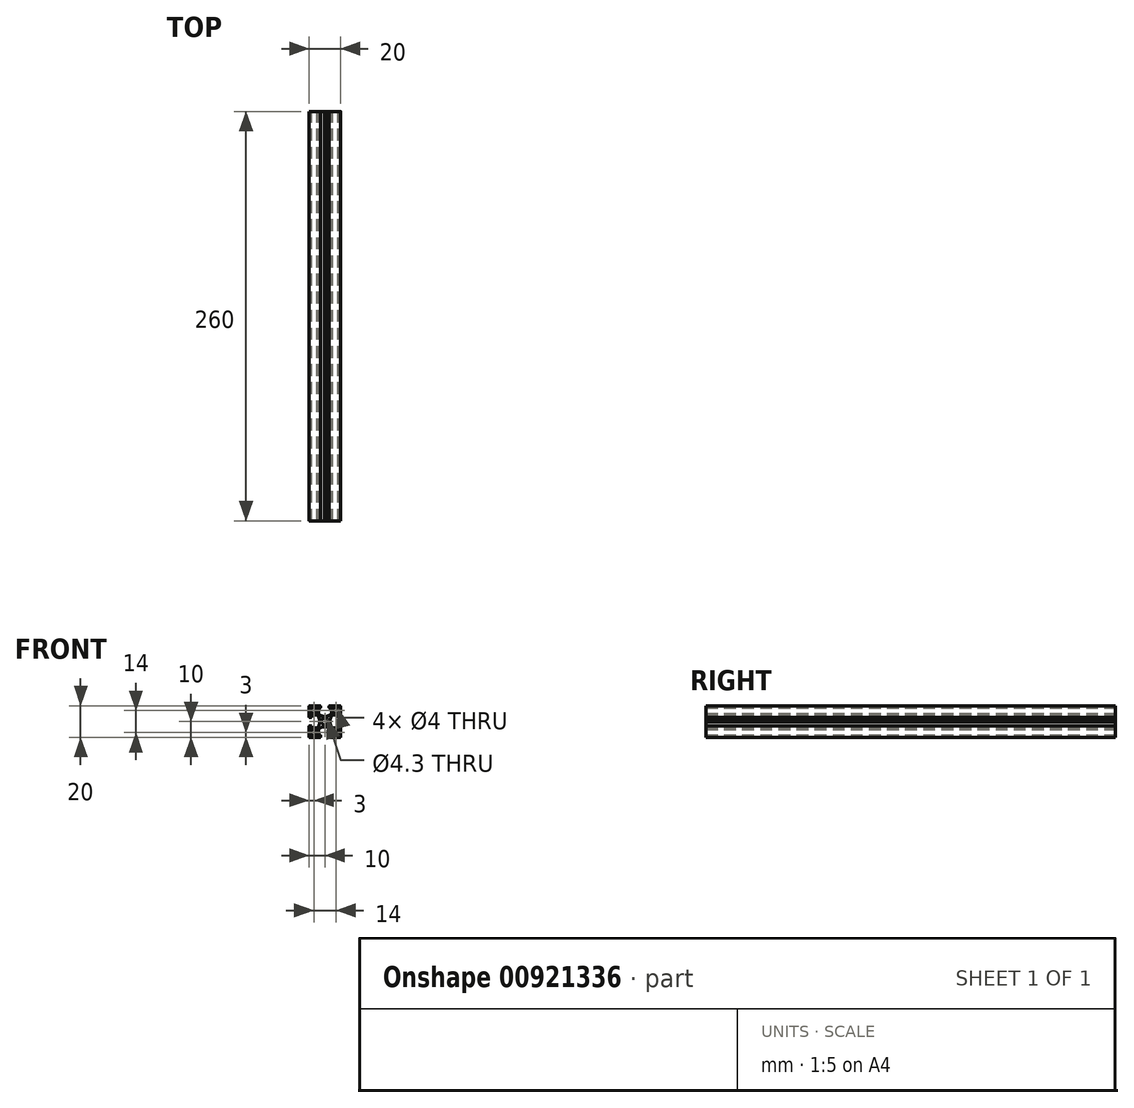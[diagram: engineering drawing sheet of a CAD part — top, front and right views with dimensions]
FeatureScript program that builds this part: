
annotation { "Feature Type Name" : "Feature", "Feature Type Description" : "" }
export const myFeature = defineFeature(function(context is Context, id is Id, definition is map)
    precondition{}
    {
        {
            var Q0;
            Q0=qCreatedBy(makeId("Front.planeOp"),FACE);
            var sketch = newSketch(context, id + "F0", { "sketchPlane" : qUnion([Q0])});
            skLineSegment(sketch, "E0", {"start": v(-11.2, 0) * mm, "end": v(11.2, 0) * mm});
            skCircle(sketch, "E1", {"center": v(0, 0) * mm, "radius": 2.15 * mm});
            skLineSegment(sketch, "E2", {"start": v(4.15, 4.94) * mm, "end": v(4.15, 8.2) * mm});
            skArc(sketch, "E3", {"start": v(4.15, 8.2) * mm, "mid": v(4.06, 8.41) * mm, "end": v(3.85, 8.5) * mm});
            skLineSegment(sketch, "E4", {"start": v(3.85, 8.5) * mm, "end": v(2.95, 8.5) * mm});
            skArc(sketch, "E5", {"start": v(2.95, 8.5) * mm, "mid": v(2.74, 8.59) * mm, "end": v(2.65, 8.8) * mm});
            skLineSegment(sketch, "E6", {"start": v(2.65, 8.8) * mm, "end": v(2.65, 9.7) * mm});
            skArc(sketch, "E7", {"start": v(2.65, 9.7) * mm, "mid": v(2.74, 9.91) * mm, "end": v(2.95, 10) * mm});
            skLineSegment(sketch, "E8", {"start": v(2.95, 10) * mm, "end": v(9.7, 10) * mm});
            skArc(sketch, "E9", {"start": v(9.7, 10) * mm, "mid": v(9.91, 9.91) * mm, "end": v(10, 9.7) * mm});
            skLineSegment(sketch, "E10", {"start": v(10, 9.7) * mm, "end": v(10, 2.95) * mm});
            skArc(sketch, "E11", {"start": v(10, 2.95) * mm, "mid": v(9.91, 2.74) * mm, "end": v(9.7, 2.65) * mm});
            skLineSegment(sketch, "E12", {"start": v(9.7, 2.65) * mm, "end": v(8.8, 2.65) * mm});
            skArc(sketch, "E13", {"start": v(8.8, 2.65) * mm, "mid": v(8.59, 2.74) * mm, "end": v(8.5, 2.95) * mm});
            skLineSegment(sketch, "E14", {"start": v(8.5, 2.95) * mm, "end": v(8.5, 3.85) * mm});
            skArc(sketch, "E15", {"start": v(8.5, 3.85) * mm, "mid": v(8.41, 4.06) * mm, "end": v(8.2, 4.15) * mm});
            skLineSegment(sketch, "E16", {"start": v(8.2, 4.15) * mm, "end": v(4.94, 4.15) * mm});
            skArc(sketch, "E17", {"start": v(4.94, 4.15) * mm, "mid": v(4.81, 4.12) * mm, "end": v(4.7, 4.04) * mm});
            skArc(sketch, "E18", {"start": v(4.7, 4.04) * mm, "mid": v(3.71, 2.28) * mm, "end": v(3.3, 0.3) * mm});
            skLineSegment(sketch, "E19", {"start": v(3.3, 0.3) * mm, "end": v(3, 0) * mm});
            skLineSegment(sketch, "E20", {"start": v(3, 0) * mm, "end": v(3.3, -0.3) * mm});
            skArc(sketch, "E21", {"start": v(3.3, -0.3) * mm, "mid": v(3.71, -2.28) * mm, "end": v(4.7, -4.04) * mm});
            skArc(sketch, "E22", {"start": v(4.7, -4.04) * mm, "mid": v(4.81, -4.12) * mm, "end": v(4.94, -4.15) * mm});
            skLineSegment(sketch, "E23", {"start": v(4.94, -4.15) * mm, "end": v(8.2, -4.15) * mm});
            skArc(sketch, "E24", {"start": v(8.2, -4.15) * mm, "mid": v(8.41, -4.06) * mm, "end": v(8.5, -3.85) * mm});
            skLineSegment(sketch, "E25", {"start": v(8.5, -3.85) * mm, "end": v(8.5, -2.95) * mm});
            skArc(sketch, "E26", {"start": v(8.5, -2.95) * mm, "mid": v(8.59, -2.74) * mm, "end": v(8.8, -2.65) * mm});
            skLineSegment(sketch, "E27", {"start": v(8.8, -2.65) * mm, "end": v(9.7, -2.65) * mm});
            skArc(sketch, "E28", {"start": v(9.7, -2.65) * mm, "mid": v(9.91, -2.74) * mm, "end": v(10, -2.95) * mm});
            skLineSegment(sketch, "E29", {"start": v(10, -2.95) * mm, "end": v(10, -9.7) * mm});
            skArc(sketch, "E30", {"start": v(10, -9.7) * mm, "mid": v(9.91, -9.91) * mm, "end": v(9.7, -10) * mm});
            skLineSegment(sketch, "E31", {"start": v(9.7, -10) * mm, "end": v(2.95, -10) * mm});
            skArc(sketch, "E32", {"start": v(2.95, -10) * mm, "mid": v(2.74, -9.91) * mm, "end": v(2.65, -9.7) * mm});
            skLineSegment(sketch, "E33", {"start": v(2.65, -9.7) * mm, "end": v(2.65, -8.8) * mm});
            skArc(sketch, "E34", {"start": v(2.65, -8.8) * mm, "mid": v(2.74, -8.59) * mm, "end": v(2.95, -8.5) * mm});
            skLineSegment(sketch, "E35", {"start": v(2.95, -8.5) * mm, "end": v(3.85, -8.5) * mm});
            skArc(sketch, "E36", {"start": v(3.85, -8.5) * mm, "mid": v(4.06, -8.41) * mm, "end": v(4.15, -8.2) * mm});
            skLineSegment(sketch, "E37", {"start": v(4.15, -8.2) * mm, "end": v(4.15, -4.94) * mm});
            skArc(sketch, "E38", {"start": v(4.15, -4.94) * mm, "mid": v(4.12, -4.81) * mm, "end": v(4.04, -4.7) * mm});
            skArc(sketch, "E39", {"start": v(4.04, -4.7) * mm, "mid": v(2.28, -3.71) * mm, "end": v(0.3, -3.3) * mm});
            skLineSegment(sketch, "E40", {"start": v(0.3, -3.3) * mm, "end": v(0, -3) * mm});
            skLineSegment(sketch, "E41", {"start": v(0, -3) * mm, "end": v(-0.3, -3.3) * mm});
            skArc(sketch, "E42", {"start": v(-0.3, -3.3) * mm, "mid": v(-2.28, -3.71) * mm, "end": v(-4.04, -4.7) * mm});
            skArc(sketch, "E43", {"start": v(-4.04, -4.7) * mm, "mid": v(-4.12, -4.81) * mm, "end": v(-4.15, -4.94) * mm});
            skLineSegment(sketch, "E44", {"start": v(-4.15, -4.94) * mm, "end": v(-4.15, -8.2) * mm});
            skArc(sketch, "E45", {"start": v(-4.15, -8.2) * mm, "mid": v(-4.06, -8.41) * mm, "end": v(-3.85, -8.5) * mm});
            skLineSegment(sketch, "E46", {"start": v(-3.85, -8.5) * mm, "end": v(-2.95, -8.5) * mm});
            skArc(sketch, "E47", {"start": v(-2.95, -8.5) * mm, "mid": v(-2.74, -8.59) * mm, "end": v(-2.65, -8.8) * mm});
            skLineSegment(sketch, "E48", {"start": v(-2.65, -8.8) * mm, "end": v(-2.65, -9.7) * mm});
            skArc(sketch, "E49", {"start": v(-2.65, -9.7) * mm, "mid": v(-2.74, -9.91) * mm, "end": v(-2.95, -10) * mm});
            skLineSegment(sketch, "E50", {"start": v(-2.95, -10) * mm, "end": v(-9.7, -10) * mm});
            skArc(sketch, "E51", {"start": v(-9.7, -10) * mm, "mid": v(-9.91, -9.91) * mm, "end": v(-10, -9.7) * mm});
            skLineSegment(sketch, "E52", {"start": v(-10, -9.7) * mm, "end": v(-10, -2.95) * mm});
            skArc(sketch, "E53", {"start": v(-10, -2.95) * mm, "mid": v(-9.91, -2.74) * mm, "end": v(-9.7, -2.65) * mm});
            skLineSegment(sketch, "E54", {"start": v(-9.7, -2.65) * mm, "end": v(-8.8, -2.65) * mm});
            skArc(sketch, "E55", {"start": v(-8.8, -2.65) * mm, "mid": v(-8.59, -2.74) * mm, "end": v(-8.5, -2.95) * mm});
            skLineSegment(sketch, "E56", {"start": v(-8.5, -2.95) * mm, "end": v(-8.5, -3.85) * mm});
            skArc(sketch, "E57", {"start": v(-8.5, -3.85) * mm, "mid": v(-8.41, -4.06) * mm, "end": v(-8.2, -4.15) * mm});
            skLineSegment(sketch, "E58", {"start": v(-8.2, -4.15) * mm, "end": v(-4.94, -4.15) * mm});
            skArc(sketch, "E59", {"start": v(-4.94, -4.15) * mm, "mid": v(-4.81, -4.12) * mm, "end": v(-4.7, -4.04) * mm});
            skArc(sketch, "E60", {"start": v(-4.7, -4.04) * mm, "mid": v(-3.71, -2.28) * mm, "end": v(-3.3, -0.3) * mm});
            skLineSegment(sketch, "E61", {"start": v(-3.3, -0.3) * mm, "end": v(-3, 0) * mm});
            skLineSegment(sketch, "E62", {"start": v(-3, 0) * mm, "end": v(-3.3, 0.3) * mm});
            skArc(sketch, "E63", {"start": v(-3.3, 0.3) * mm, "mid": v(-3.71, 2.28) * mm, "end": v(-4.7, 4.04) * mm});
            skArc(sketch, "E64", {"start": v(-4.7, 4.04) * mm, "mid": v(-4.81, 4.12) * mm, "end": v(-4.94, 4.15) * mm});
            skLineSegment(sketch, "E65", {"start": v(-4.94, 4.15) * mm, "end": v(-8.2, 4.15) * mm});
            skArc(sketch, "E66", {"start": v(-8.2, 4.15) * mm, "mid": v(-8.41, 4.06) * mm, "end": v(-8.5, 3.85) * mm});
            skLineSegment(sketch, "E67", {"start": v(-8.5, 3.85) * mm, "end": v(-8.5, 2.95) * mm});
            skArc(sketch, "E68", {"start": v(-8.5, 2.95) * mm, "mid": v(-8.59, 2.74) * mm, "end": v(-8.8, 2.65) * mm});
            skLineSegment(sketch, "E69", {"start": v(-8.8, 2.65) * mm, "end": v(-9.7, 2.65) * mm});
            skArc(sketch, "E70", {"start": v(-9.7, 2.65) * mm, "mid": v(-9.91, 2.74) * mm, "end": v(-10, 2.95) * mm});
            skLineSegment(sketch, "E71", {"start": v(-10, 2.95) * mm, "end": v(-10, 9.7) * mm});
            skArc(sketch, "E72", {"start": v(-10, 9.7) * mm, "mid": v(-9.91, 9.91) * mm, "end": v(-9.7, 10) * mm});
            skLineSegment(sketch, "E73", {"start": v(-9.7, 10) * mm, "end": v(-2.95, 10) * mm});
            skArc(sketch, "E74", {"start": v(-2.95, 10) * mm, "mid": v(-2.74, 9.91) * mm, "end": v(-2.65, 9.7) * mm});
            skLineSegment(sketch, "E75", {"start": v(-2.65, 9.7) * mm, "end": v(-2.65, 8.8) * mm});
            skArc(sketch, "E76", {"start": v(-2.65, 8.8) * mm, "mid": v(-2.74, 8.59) * mm, "end": v(-2.95, 8.5) * mm});
            skLineSegment(sketch, "E77", {"start": v(-2.95, 8.5) * mm, "end": v(-3.85, 8.5) * mm});
            skArc(sketch, "E78", {"start": v(-3.85, 8.5) * mm, "mid": v(-4.06, 8.41) * mm, "end": v(-4.15, 8.2) * mm});
            skLineSegment(sketch, "E79", {"start": v(-4.15, 8.2) * mm, "end": v(-4.15, 4.94) * mm});
            skArc(sketch, "E80", {"start": v(-4.15, 4.94) * mm, "mid": v(-4.12, 4.81) * mm, "end": v(-4.04, 4.7) * mm});
            skArc(sketch, "E81", {"start": v(-4.04, 4.7) * mm, "mid": v(-2.28, 3.71) * mm, "end": v(-0.3, 3.3) * mm});
            skLineSegment(sketch, "E82", {"start": v(-0.3, 3.3) * mm, "end": v(0, 3) * mm});
            skLineSegment(sketch, "E83", {"start": v(0, 3) * mm, "end": v(0.3, 3.3) * mm});
            skArc(sketch, "E84", {"start": v(0.3, 3.3) * mm, "mid": v(2.28, 3.71) * mm, "end": v(4.04, 4.7) * mm});
            skArc(sketch, "E85", {"start": v(4.04, 4.7) * mm, "mid": v(4.12, 4.81) * mm, "end": v(4.15, 4.94) * mm});
            skLineSegment(sketch, "E86", {"start": v(-9.5, 7) * mm, "end": v(-4.5, 7) * mm});
            skLineSegment(sketch, "E87", {"start": v(-7, 9.5) * mm, "end": v(-7, 4.5) * mm});
            skCircle(sketch, "E88", {"center": v(-7, 7) * mm, "radius": 2 * mm});
            skLineSegment(sketch, "E89", {"start": v(-9.5, -7) * mm, "end": v(-4.5, -7) * mm});
            skLineSegment(sketch, "E90", {"start": v(-7, -9.5) * mm, "end": v(-7, -4.5) * mm});
            skCircle(sketch, "E91", {"center": v(-7, -7) * mm, "radius": 2 * mm});
            skLineSegment(sketch, "E92", {"start": v(0, 11.2) * mm, "end": v(0, -11.2) * mm});
            skLineSegment(sketch, "E93", {"start": v(9.5, 7) * mm, "end": v(4.5, 7) * mm});
            skLineSegment(sketch, "E94", {"start": v(7, 9.5) * mm, "end": v(7, 4.5) * mm});
            skCircle(sketch, "E95", {"center": v(7, 7) * mm, "radius": 2 * mm});
            skCircle(sketch, "E96", {"center": v(7, -7) * mm, "radius": 2 * mm});
            skLineSegment(sketch, "E97", {"start": v(7, -9.5) * mm, "end": v(7, -4.5) * mm});
            skLineSegment(sketch, "E98", {"start": v(9.5, -7) * mm, "end": v(4.5, -7) * mm});
            skSolve(sketch);
        }
        {
            var Q0;
            {var subQ0=sQuery(id+"F0.wireOp",EDGE,"E62");Q0=makeQuery(id+"F0.imprint","IMPRINT",FACE,{"disambiguationData":[TD([[makeQuery(id+"F0.imprint","IMPRINT",EDGE,{"derivedFrom":subQ0}),-1.0]])]});}
            var Q1;
            Q1=makeQuery(id+"F0.imprint","IMPRINT",FACE,{"disambiguationData":[TD([[makeQuery(id+"F0.imprint","IMPRINT",EDGE,{"derivedFrom":sQuery(id+"F0.wireOp",EDGE,"E2")}),-1.0]])]});
            var Q2;
            {var subQ10=sQuery(id+"F0.wireOp",EDGE,"E20");Q2=makeQuery(id+"F0.imprint","IMPRINT",FACE,{"disambiguationData":[TD([[makeQuery(id+"F0.imprint","IMPRINT",EDGE,{"derivedFrom":subQ10}),-1.0]])]});}
            var Q3;
            {var subQ1=sQuery(id+"F0.wireOp",EDGE,"E41");Q3=makeQuery(id+"F0.imprint","IMPRINT",FACE,{"disambiguationData":[TD([[makeQuery(id+"F0.imprint","IMPRINT",EDGE,{"derivedFrom":subQ1}),-1.0]])]});}
            extrude(context, id + "F1", {"entities" : qUnion([Q0, Q1, Q2, Q3]), "depth" : 260 * mm, "offsetDistance" : 25 * mm});
        }
    });
